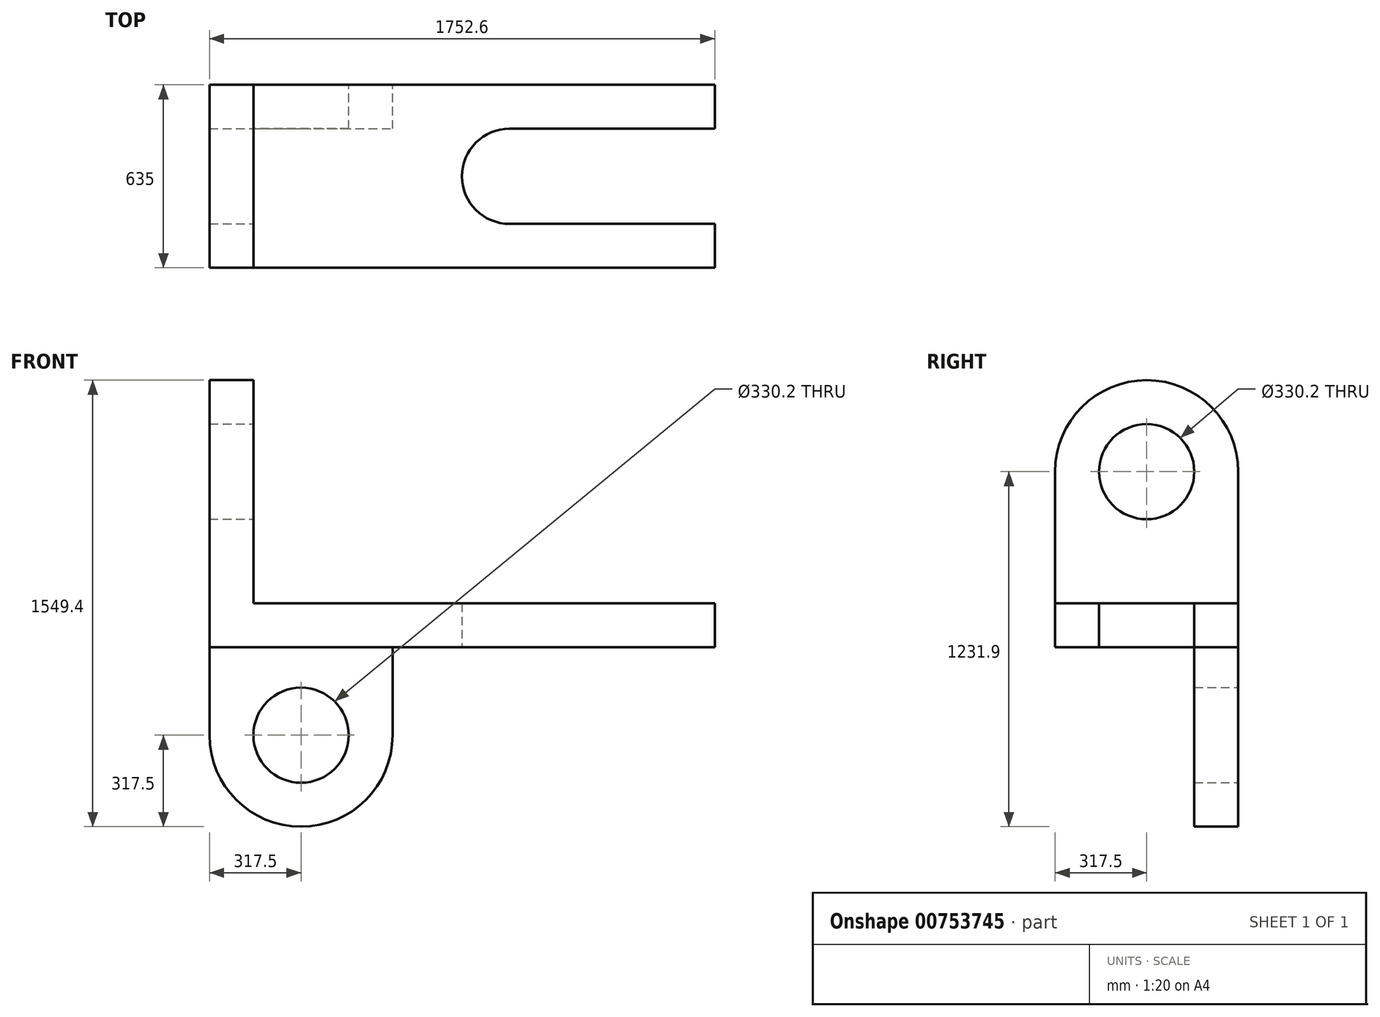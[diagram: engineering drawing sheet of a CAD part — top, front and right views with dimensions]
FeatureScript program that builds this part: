
annotation { "Feature Type Name" : "Feature", "Feature Type Description" : "" }
export const myFeature = defineFeature(function(context is Context, id is Id, definition is map)
    precondition{}
    {
        {
            var Q0;
            Q0=qCreatedBy(makeId("Top.planeOp"),FACE);
            var sketch = newSketch(context, id + "F0", { "sketchPlane" : qUnion([Q0])});
            skLineSegment(sketch, "E0.bottom", {"start": v(0, 0) * mm, "end": v(1752.6, 0) * mm});
            skLineSegment(sketch, "E0.top", {"start": v(0, 635) * mm, "end": v(1752.6, 635) * mm});
            skLineSegment(sketch, "E0.left", {"start": v(0, 0) * mm, "end": v(0, 635) * mm});
            skLineSegment(sketch, "E0.right", {"start": v(1752.6, 0) * mm, "end": v(1752.6, 635) * mm});
            skLineSegment(sketch, "E1", {"start": v(1752.6, 482.6) * mm, "end": v(1040.84, 482.6) * mm});
            skLineSegment(sketch, "E2", {"start": v(1040.84, 152.4) * mm, "end": v(1752.6, 152.4) * mm});
            skArc(sketch, "E3", {"start": v(1040.84, 482.6) * mm, "mid": v(875.74, 317.5) * mm, "end": v(1040.84, 152.4) * mm});
            skSolve(sketch);
        }
        {
            var Q0;
            {var subQ1=sQuery(id+"F0.wireOp",EDGE,"E0.bottom");Q0=makeQuery(id+"F0.imprint","IMPRINT",FACE,{"disambiguationData":[TD([[makeQuery(id+"F0.imprint","IMPRINT",EDGE,{"derivedFrom":subQ1}),1.0]])]});}
            extrude(context, id + "F1", {"entities" : qUnion([Q0]), "depth" : 152.4 * mm, "offsetDistance" : 25.4 * mm});
        }
        {
            var Q0;
            Q0=qCreatedBy(makeId("Right.planeOp"),FACE);
            cPlane(context, id + "F2", {"entities" : qUnion([Q0]), "cplaneType" : CPlaneType.OFFSET, "offset" : 152.4 * mm, "width" : 152.4 * mm, "height" : 152.4 * mm});
        }
        {
            var Q0;
            Q0=qCreatedBy(id+"F2.planeOp",FACE);
            var sketch = newSketch(context, id + "F3", { "sketchPlane" : qUnion([Q0])});
            skLineSegment(sketch, "E4", {"start": v(0, 0) * mm, "end": v(635, 0) * mm});
            skLineSegment(sketch, "E5", {"start": v(0, 152.4) * mm, "end": v(635, 152.4) * mm});
            skLineSegment(sketch, "E6", {"start": v(635, 152.4) * mm, "end": v(635, 609.6) * mm});
            skLineSegment(sketch, "E7", {"start": v(0, 152.4) * mm, "end": v(0, 609.6) * mm});
            skCircle(sketch, "E8", {"center": v(317.5, 609.6) * mm, "radius": 165.1 * mm});
            skArc(sketch, "E9", {"start": v(635, 609.6) * mm, "mid": v(317.5, 927.1) * mm, "end": v(0, 609.6) * mm});
            skSolve(sketch);
        }
        {
            var Q0;
            Q0=makeQuery(id+"F3.imprint","IMPRINT",FACE,{"disambiguationData":[TD([[makeQuery(id+"F3.imprint","IMPRINT",EDGE,{"derivedFrom":sQuery(id+"F3.wireOp",EDGE,"E5")}),1.0]])]});
            extrude(context, id + "F4", {"entities" : qUnion([Q0]), "operationType" : NewBodyOperationType.ADD, "oppositeDirection" : true, "depth" : 152.4 * mm, "offsetDistance" : 25.4 * mm});
        }
        {
            var Q0;
            Q0=qCreatedBy(makeId("Front.planeOp"),FACE);
            cPlane(context, id + "F5", {"entities" : qUnion([Q0]), "cplaneType" : CPlaneType.OFFSET, "offset" : 635 * mm, "oppositeDirection" : true, "width" : 152.4 * mm, "height" : 152.4 * mm});
        }
        {
            var Q0;
            Q0=qCreatedBy(id+"F5.planeOp",FACE);
            var sketch = newSketch(context, id + "F6", { "sketchPlane" : qUnion([Q0])});
            skLineSegment(sketch, "E10.bottom", {"start": v(0, 0) * mm, "end": v(635, 0) * mm});
            skLineSegment(sketch, "E10.left", {"start": v(0, 0) * mm, "end": v(0, -304.8) * mm});
            skLineSegment(sketch, "E10.right", {"start": v(635, 0) * mm, "end": v(635, -304.8) * mm});
            skCircle(sketch, "E11", {"center": v(317.5, -304.8) * mm, "radius": 165.1 * mm});
            skArc(sketch, "E12", {"start": v(0, -304.8) * mm, "mid": v(317.5, -622.3) * mm, "end": v(635, -304.8) * mm});
            skSolve(sketch);
        }
        {
            var Q0;
            Q0=makeQuery(id+"F6.imprint","IMPRINT",FACE,{"disambiguationData":[TD([[makeQuery(id+"F6.imprint","IMPRINT",EDGE,{"derivedFrom":sQuery(id+"F6.wireOp",EDGE,"E10.bottom")}),-1.0]])]});
            extrude(context, id + "F7", {"entities" : qUnion([Q0]), "operationType" : NewBodyOperationType.ADD, "depth" : 152.4 * mm, "offsetDistance" : 25.4 * mm});
        }
    });
